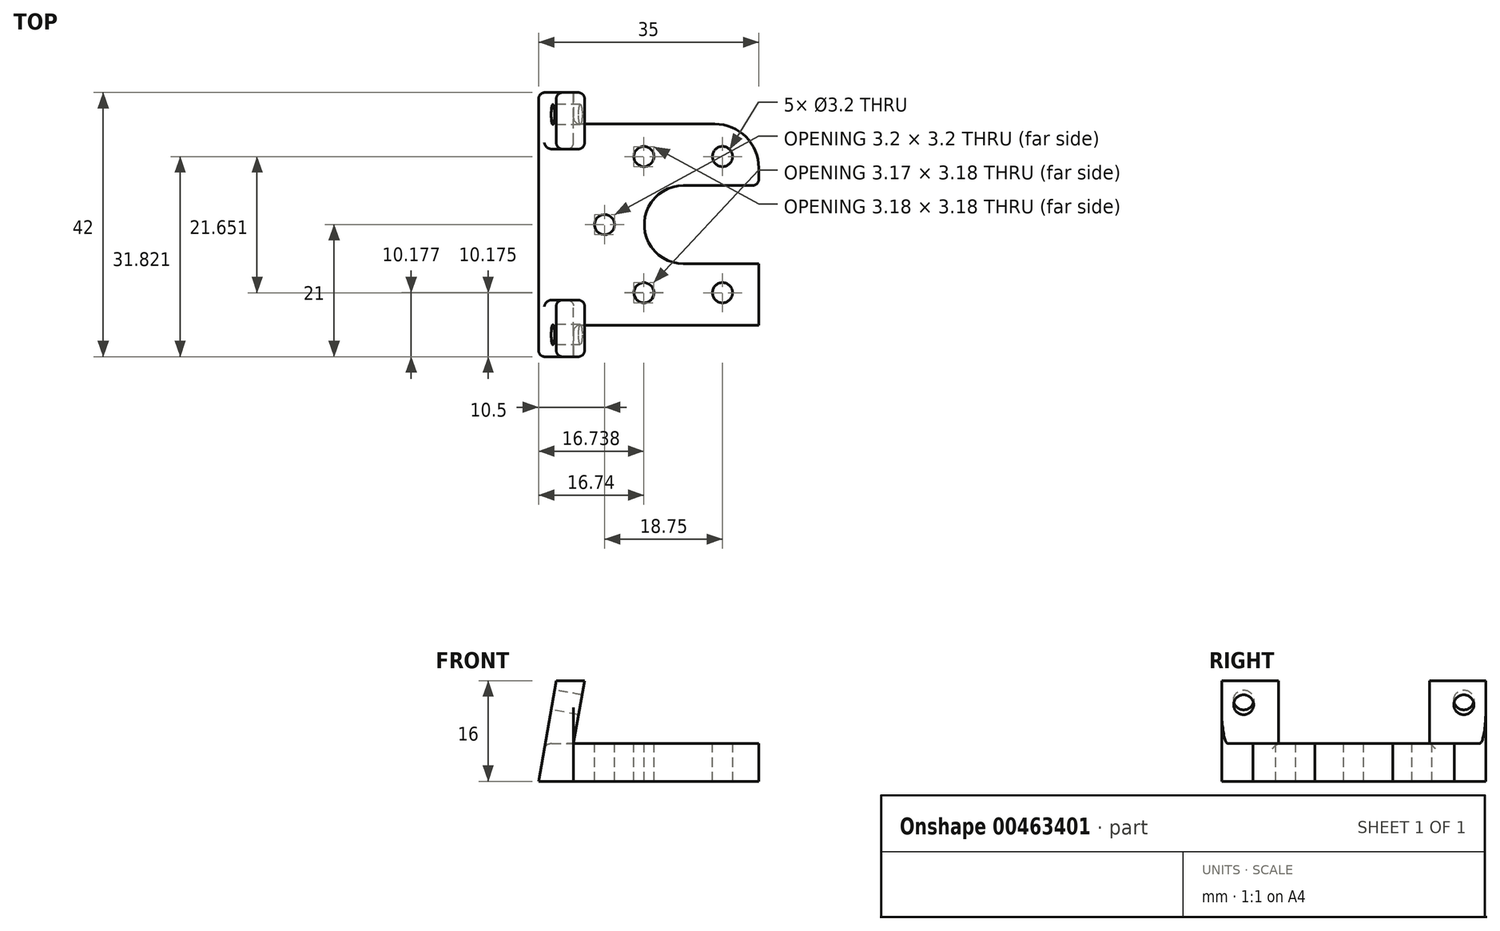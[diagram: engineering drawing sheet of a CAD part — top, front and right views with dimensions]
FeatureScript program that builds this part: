
annotation { "Feature Type Name" : "Feature", "Feature Type Description" : "" }
export const myFeature = defineFeature(function(context is Context, id is Id, definition is map)
    precondition{}
    {
        {
            var Q0;
            Q0=qCreatedBy(makeId("Front.planeOp"),FACE);
            var sketch = newSketch(context, id + "F0", { "sketchPlane" : qUnion([Q0])});
            skLineSegment(sketch, "E0", {"start": v(12, 0) * mm, "end": v(-23, 0) * mm});
            skLineSegment(sketch, "E1", {"start": v(-23, 0) * mm, "end": v(-20.18, 16) * mm});
            skLineSegment(sketch, "E2", {"start": v(-20.18, 16) * mm, "end": v(-15.68, 16) * mm});
            skLineSegment(sketch, "E3", {"start": v(-15.68, 16) * mm, "end": v(-17.44, 6) * mm});
            skLineSegment(sketch, "E4", {"start": v(-17.44, 6) * mm, "end": v(12, 6) * mm});
            skLineSegment(sketch, "E5", {"start": v(12, 6) * mm, "end": v(12, 0) * mm});
            skSolve(sketch);
        }
        {
            var Q0;
            Q0=makeQuery(id+"F0.imprint","IMPRINT",FACE,{"disambiguationData":[TD([[makeQuery(id+"F0.imprint","IMPRINT",EDGE,{"derivedFrom":sQuery(id+"F0.wireOp",EDGE,"E0")}),-1.0]])]});
            extrude(context, id + "F1", {"entities" : qUnion([Q0]), "endBound" : BoundingType.SYMMETRIC, "depth" : 42 * mm});
        }
        {
            var Q0;
            Q0=makeQuery(id+"F1.opExtrude","SWEPT_FACE",FACE,{"disambiguationData":[OSD([sQuery(id+"F0.wireOp",EDGE,"E4")])]});
            var sketch = newSketch(context, id + "F2", { "sketchPlane" : qUnion([Q0])});
            skCircle(sketch, "E6", {"center": v(0, 0) * mm, "radius": 6.2 * mm});
            skLineSegment(sketch, "E7.bottom", {"start": v(0, 6.2) * mm, "end": v(12, 6.2) * mm});
            skLineSegment(sketch, "E7.top", {"start": v(0, -6.2) * mm, "end": v(12, -6.2) * mm});
            skLineSegment(sketch, "E7.left", {"start": v(0, 6.2) * mm, "end": v(0, -6.2) * mm});
            skLineSegment(sketch, "E7.right", {"start": v(12, 6.2) * mm, "end": v(12, -6.2) * mm});
            skLineSegment(sketch, "E8.bottom", {"start": v(0, -6.2) * mm, "end": v(0, -6.2) * mm});
            skCircle(sketch, "E9", {"center": v(-12.5, 0) * mm, "radius": 1.6 * mm});
            skCircle(sketch, "E10.1.0", {"center": v(-6.25, -10.83) * mm, "radius": 1.6 * mm});
            skCircle(sketch, "E10.2.0", {"center": v(6.25, -10.83) * mm, "radius": 1.6 * mm});
            skCircle(sketch, "E10.3.0", {"center": v(12.5, 0) * mm, "radius": 1.6 * mm});
            skCircle(sketch, "E10.4.0", {"center": v(6.25, 10.83) * mm, "radius": 1.6 * mm});
            skCircle(sketch, "E10.5.0", {"center": v(-6.25, 10.83) * mm, "radius": 1.6 * mm});
            skLineSegment(sketch, "E11.bottom", {"start": v(-17.44, 21) * mm, "end": v(12, 21) * mm});
            skLineSegment(sketch, "E11.top", {"start": v(-17.44, 16) * mm, "end": v(12, 16) * mm});
            skLineSegment(sketch, "E11.left", {"start": v(-17.44, 21) * mm, "end": v(-17.44, 16) * mm});
            skLineSegment(sketch, "E11.right", {"start": v(12, 21) * mm, "end": v(12, 16) * mm});
            skLineSegment(sketch, "E12.MirrorCS", {"start": v(12, -21) * mm, "end": v(12, -16) * mm});
            skLineSegment(sketch, "E13.MirrorCS", {"start": v(-17.44, -16) * mm, "end": v(12, -16) * mm});
            skLineSegment(sketch, "E14.MirrorCS", {"start": v(-17.44, -21) * mm, "end": v(12, -21) * mm});
            skLineSegment(sketch, "E15.MirrorCS", {"start": v(-17.44, -21) * mm, "end": v(-17.44, -16) * mm});
            skSolve(sketch);
        }
        {
            var Q0;
            Q0 = qSketchRegion(id + "F2", true);
            extrude(context, id + "F3", {"entities" : qUnion([Q0]), "operationType" : NewBodyOperationType.REMOVE, "endBound" : BoundingType.THROUGH_ALL, "oppositeDirection" : true, "depth" : 25 * mm});
        }
        {
            var Q0;
            Q0=makeQuery(id+"F1.opExtrude","SWEPT_FACE",FACE,{"disambiguationData":[OSD([sQuery(id+"F0.wireOp",EDGE,"E1")])]});
            var sketch = newSketch(context, id + "F4", { "sketchPlane" : qUnion([Q0])});
            skCircle(sketch, "E16", {"center": v(-17.5, 9.15) * mm, "radius": 1.6 * mm});
            skLineSegment(sketch, "E17", {"start": v(0, 12.25) * mm, "end": v(0, 0) * mm, "construction": true});
            skCircle(sketch, "E18.MirrorC", {"center": v(17.5, 9.15) * mm, "radius": 1.6 * mm});
            skSolve(sketch);
        }
        {
            var Q0;
            Q0 = qSketchRegion(id + "F4", true);
            var Q1;
            Q1=makeQuery(id+"F1.opExtrude","SWEPT_FACE",FACE,{"disambiguationData":[OSD([sQuery(id+"F0.wireOp",EDGE,"E3")])]});
            extrude(context, id + "F5", {"entities" : qUnion([Q0]), "operationType" : NewBodyOperationType.REMOVE, "endBound" : BoundingType.UP_TO_SURFACE, "oppositeDirection" : true, "endBoundEntityFace" : qUnion([Q1]), "depth" : 25 * mm});
        }
        {
            var Q0;
            Q0=qCreatedBy(makeId("Right.planeOp"),FACE);
            var sketch = newSketch(context, id + "F6", { "sketchPlane" : qUnion([Q0])});
            skLineSegment(sketch, "E19.bottom", {"start": v(-11.99, 16) * mm, "end": v(12.01, 16) * mm});
            skLineSegment(sketch, "E19.top", {"start": v(-11.99, 6) * mm, "end": v(12.01, 6) * mm});
            skLineSegment(sketch, "E19.left", {"start": v(-11.99, 16) * mm, "end": v(-11.99, 6) * mm});
            skLineSegment(sketch, "E19.right", {"start": v(12.01, 16) * mm, "end": v(12.01, 6) * mm});
            skSolve(sketch);
        }
        {
            var Q0;
            Q0 = qSketchRegion(id + "F6", true);
            extrude(context, id + "F7", {"entities" : qUnion([Q0]), "operationType" : NewBodyOperationType.REMOVE, "endBound" : BoundingType.THROUGH_ALL, "oppositeDirection" : true, "depth" : 25 * mm});
        }
        {
            var Q0;
            Q0=makeQuery(id+"F3.boolean.opBoolean","COPY",EDGE,{"derivedFrom":makeQuery(id+"F3.opExtrude","SWEPT_EDGE",EDGE,{"disambiguationData":[OSD([sQuery(id+"F0.wireOp",EDGE,"E4"),sQuery(id+"F0.wireOp",EDGE,"E5"),sQuery(id+"F2.wireOp",EDGE,"E7.top"),sQuery(id+"F2.wireOp",EDGE,"E7.right")])]})});
            var Q1;
            Q1=makeQuery(id+"F3.boolean.opBoolean","COPY",EDGE,{"derivedFrom":makeQuery(id+"F3.opExtrude","SWEPT_EDGE",EDGE,{"disambiguationData":[OSD([sQuery(id+"F0.wireOp",EDGE,"E4"),sQuery(id+"F0.wireOp",EDGE,"E5"),sQuery(id+"F2.wireOp",EDGE,"E7.bottom"),sQuery(id+"F2.wireOp",EDGE,"E7.right")])]})});
            var Q2;
            Q2=makeQuery(id+"F1.opExtrude","CAP_EDGE",EDGE,{"disambiguationData":[OSD([sQuery(id+"F0.wireOp",EDGE,"E3")])],"isStart":false});
            var Q3;
            Q3=makeQuery(id+"F1.opExtrude","CAP_EDGE",EDGE,{"disambiguationData":[OSD([sQuery(id+"F0.wireOp",EDGE,"E3")])],"isStart":true});
            var Q4;
            Q4=makeQuery(id+"F7.boolean.opBoolean","INTERSECT",EDGE,{"derivedFrom":[makeQuery(id+"F1.opExtrude","SWEPT_FACE",FACE,{"disambiguationData":[OSD([sQuery(id+"F0.wireOp",EDGE,"E3")])]}),makeQuery(id+"F7.opExtrude","SWEPT_FACE",FACE,{"disambiguationData":[OSD([sQuery(id+"F6.wireOp",EDGE,"E19.right")])]})]});
            var Q5;
            Q5=makeQuery(id+"F7.boolean.opBoolean","INTERSECT",EDGE,{"derivedFrom":[makeQuery(id+"F1.opExtrude","SWEPT_FACE",FACE,{"disambiguationData":[OSD([sQuery(id+"F0.wireOp",EDGE,"E3")])]}),makeQuery(id+"F7.opExtrude","SWEPT_FACE",FACE,{"disambiguationData":[OSD([sQuery(id+"F6.wireOp",EDGE,"E19.left")])]})]});
            var Q6;
            Q6=makeQuery(id+"F7.boolean.opBoolean","INTERSECT",EDGE,{"derivedFrom":[makeQuery(id+"F1.opExtrude","SWEPT_FACE",FACE,{"disambiguationData":[OSD([sQuery(id+"F0.wireOp",EDGE,"E1")])]}),makeQuery(id+"F7.opExtrude","SWEPT_FACE",FACE,{"disambiguationData":[OSD([sQuery(id+"F6.wireOp",EDGE,"E19.right")])]})]});
            var Q7;
            Q7=makeQuery(id+"F1.opExtrude","CAP_EDGE",EDGE,{"disambiguationData":[OSD([sQuery(id+"F0.wireOp",EDGE,"E1")])],"isStart":false});
            var Q8;
            Q8=makeQuery(id+"F7.boolean.opBoolean","INTERSECT",EDGE,{"derivedFrom":[makeQuery(id+"F1.opExtrude","SWEPT_FACE",FACE,{"disambiguationData":[OSD([sQuery(id+"F0.wireOp",EDGE,"E1")])]}),makeQuery(id+"F7.opExtrude","SWEPT_FACE",FACE,{"disambiguationData":[OSD([sQuery(id+"F6.wireOp",EDGE,"E19.left")])]})]});
            var Q9;
            Q9=makeQuery(id+"F1.opExtrude","CAP_EDGE",EDGE,{"disambiguationData":[OSD([sQuery(id+"F0.wireOp",EDGE,"E1")])],"isStart":true});
            var Q10;
            Q10=makeQuery(id+"F3.boolean.opBoolean","COPY",EDGE,{"derivedFrom":makeQuery(id+"F3.opExtrude","SWEPT_EDGE",EDGE,{"disambiguationData":[OSD([sQuery(id+"F2.wireOp",EDGE,"E14.MirrorCS"),sQuery(id+"F2.wireOp",EDGE,"E15.MirrorCS")])]})});
            var Q11;
            Q11=makeQuery(id+"F3.boolean.opBoolean","COPY",EDGE,{"derivedFrom":makeQuery(id+"F3.opExtrude","SWEPT_EDGE",EDGE,{"disambiguationData":[OSD([sQuery(id+"F2.wireOp",EDGE,"E11.bottom"),sQuery(id+"F2.wireOp",EDGE,"E11.left")])]})});
            var Q12;
            Q12=makeQuery(id+"F3.boolean.opBoolean","COPY",EDGE,{"derivedFrom":makeQuery(id+"F3.opExtrude","SWEPT_EDGE",EDGE,{"disambiguationData":[OSD([sQuery(id+"F0.wireOp",EDGE,"E3"),sQuery(id+"F0.wireOp",EDGE,"E4"),sQuery(id+"F2.wireOp",EDGE,"E13.MirrorCS"),sQuery(id+"F2.wireOp",EDGE,"E15.MirrorCS")])]})});
            var Q13;
            Q13=makeQuery(id+"F3.boolean.opBoolean","COPY",EDGE,{"derivedFrom":makeQuery(id+"F3.opExtrude","SWEPT_EDGE",EDGE,{"disambiguationData":[OSD([sQuery(id+"F0.wireOp",EDGE,"E3"),sQuery(id+"F0.wireOp",EDGE,"E4"),sQuery(id+"F2.wireOp",EDGE,"E11.top"),sQuery(id+"F2.wireOp",EDGE,"E11.left")])]})});
            var Q14;
            Q14=makeQuery(id+"F7.boolean.opBoolean","INTERSECT",EDGE,{"derivedFrom":[makeQuery(id+"F1.opExtrude","SWEPT_FACE",FACE,{"disambiguationData":[OSD([sQuery(id+"F0.wireOp",EDGE,"E1")])]}),makeQuery(id+"F7.opExtrude","SWEPT_FACE",FACE,{"disambiguationData":[OSD([sQuery(id+"F6.wireOp",EDGE,"E19.top")])]})]});
            fillet(context, id + "F8", {"entities" : qUnion([Q0, Q1, Q2, Q3, Q4, Q5, Q6, Q7, Q8, Q9, Q10, Q11, Q12, Q13, Q14]), "radius" : 1 * mm, "tangentPropagation" : true, "allowEdgeOverflow" : false});
        }
        {
            var Q0;
            Q0=makeQuery(id+"F3.boolean.opBoolean","COPY",EDGE,{"derivedFrom":makeQuery(id+"F3.opExtrude","SWEPT_EDGE",EDGE,{"disambiguationData":[OSD([sQuery(id+"F0.wireOp",EDGE,"E4"),sQuery(id+"F0.wireOp",EDGE,"E5"),sQuery(id+"F2.wireOp",EDGE,"E11.top"),sQuery(id+"F2.wireOp",EDGE,"E11.right")])]})});
            var Q1;
            Q1=makeQuery(id+"F3.boolean.opBoolean","COPY",EDGE,{"derivedFrom":makeQuery(id+"F3.opExtrude","SWEPT_EDGE",EDGE,{"disambiguationData":[OSD([sQuery(id+"F0.wireOp",EDGE,"E4"),sQuery(id+"F0.wireOp",EDGE,"E5"),sQuery(id+"F2.wireOp",EDGE,"E12.MirrorCS"),sQuery(id+"F2.wireOp",EDGE,"E13.MirrorCS")])]})});
            fillet(context, id + "F9", {"entities" : qUnion([Q0, Q1]), "radius" : 7 * mm, "tangentPropagation" : true, "allowEdgeOverflow" : false});
        }
    });
